MODEL slx_56b5187626d2
CONFIG AbsTol = auto
CONFIG EnableMultiTasking = off
CONFIG FixedStep = auto
CONFIG MaxStep = auto
CONFIG MinStep = auto
CONFIG RelTol = 1e-3
CONFIG SampleTimeConstraint = Unconstrained
CONFIG Solver = VariableStepAuto
CONFIG SolverName = VariableStepAuto
CONFIG StartTime = 0.0
CONFIG StopTime = 10.0
BLOCK [Reference] PID Controller  REF=simulink/Continuous/PID Controller
  Ports = [1, 1]
  SourceBlock = simulink/Continuous/PID Controller
  SourceProductBaseCode = SL
  SourceType = PID 1dof
BLOCK [Scope] Scope
  Floating = off
  NumInputPorts = 1
  Ports = [1]
  ScopeSpecificationString = Simulink.scopes.TimeScopeBlockCfg('CurrentConfiguration', extmgr.ConfigurationSet(extmgr.Configuration('Core','General UI',true),extmgr.Configuration('Core','Source UI',true),extmgr.Configuration('Sources','WiredSimulink',true),extmgr.Configuration('Visuals','Time Domain',true,'SerializedDisplays',{struct('MinYLimReal','-0.12513','MaxYLimReal','1.12619','YLabelReal','','MinYLimMag','0.00000','MaxY...<+1413ch>
BLOCK [Step] Step
  SampleTime = 0
BLOCK [Sum] Sum
  Inputs = |+-
  Ports = [2, 1]
BLOCK [TransferFcn] Transfer Fcn
  Denominator = [1 5 31]
LINE PID Controller:1 -> Transfer Fcn:1
LINE Step:1 -> Sum:1
LINE Sum:1 -> PID Controller:1
LINE Transfer Fcn:1 -> Scope:1
LINE Transfer Fcn:1 -> Sum:2
